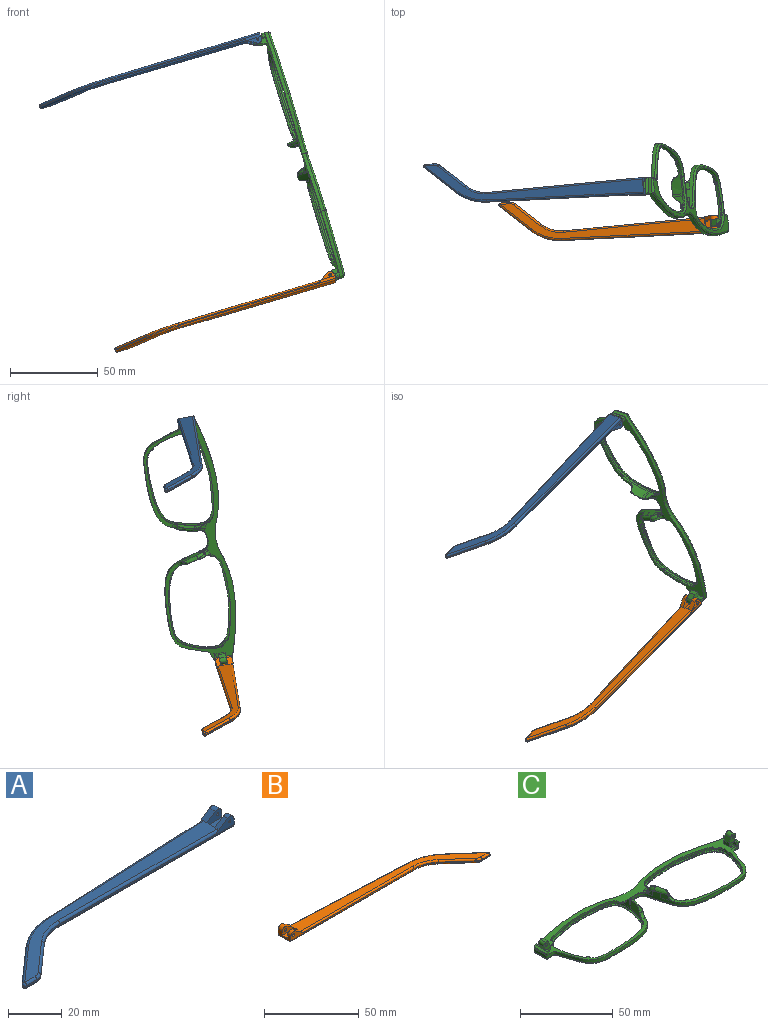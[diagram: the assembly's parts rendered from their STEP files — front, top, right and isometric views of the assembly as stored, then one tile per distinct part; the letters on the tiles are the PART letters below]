
ASSEMBLY  parts=3 mates=2
PART A: 43 faces, bbox 130.2x29.5x5.9 mm
  f0: plane 9.62x3.72mm, normal (1,0,0), area 24.7mm2, adj f1,f3,f4,f5,f10,f16,f18,f28
  f1: cylinder r=2.2mm len=3.45mm, axis (0,-1,0), area 11mm2, adj f0,f2,f4,f37
  f2: plane 6.01x3.91mm, normal (-0.55,0,0.84), area 12.7mm2, adj f1,f4,f9,f19,f37
  f3: plane 2.26x0.1mm, normal (0,0,1), area 0.1mm2, adj f0,f5,f18
  f4: plane 92.1x4.9mm, normal (0,-1,0), area 79.9mm2, adj f0,f1,f2,f14,f19,f36,f42
  f5: plane 93.42x4.13mm, normal (-0.04,1,0), area 64.8mm2, adj f0,f3,f11,f15,f17,f27,f28
  f6: plane 17.82x15.72mm, normal (-0.66,0.75,0), area 14.3mm2, adj f11,f12,f25,f30
  f7: plane 5.46x0.6mm, normal (0,-1,0), area 3.3mm2, adj f12,f13,f23,f32
  f8: plane 14.99x13.23mm, normal (0.66,-0.75,0), area 12mm2, adj f13,f14,f21,f34
  f9: plane 121.18x26.73mm, normal (0,0,1), area 627.7mm2, adj f2,f17,f19,f20,f21,f22,f23,f25
  f10: plane 129.1x27.08mm, normal (0,0,-1), area 686.5mm2, adj f0,f28,f29,f30,f32,f33,f34,f35
  f11: cylinder r=30mm len=18.52mm, axis (0,0,-1), area 12.2mm2, adj f5,f6,f26,f29
  f12: cylinder r=1mm len=1.75mm, axis (0,0,-1), area 1.5mm2, adj f6,f7,f24,f31
  f13: cylinder r=5mm len=3.31mm, axis (0,0,-1), area 2.2mm2, adj f7,f8,f22,f33
  f14: cylinder r=20mm len=13.23mm, axis (0,0,1), area 8.7mm2, adj f4,f8,f20,f35
  f15: plane 5.66x0.25mm, normal (0,0,-1), area 0.7mm2, adj f5,f17,f18
  f16: cylinder r=2.2mm len=3.45mm, axis (0,-1,0), area 14.8mm2, adj f0,f17,f18,f38
  f17: plane 6.01x3.91mm, normal (-0.55,0,0.84), area 16.9mm2, adj f5,f9,f15,f16,f18,f27,f38
  f18: plane 7.92x3.3mm, normal (0,1,0), area 15.9mm2, adj f0,f3,f15,f16,f17,f41
  f19: cylinder r=1mm len=84.18mm, axis (-1,0,0), area 131.4mm2, adj f2,f4,f9,f20
  f20: torus R=21mm, axis (0,0,1), area 23.1mm2, adj f9,f14,f19,f21
  f21: cylinder r=1mm len=15.65mm, axis (-0.75,-0.66,0), area 31.4mm2, adj f8,f9,f20,f22
  f22: torus R=4mm, axis (0,0,1), area 5.3mm2, adj f9,f13,f21,f23
  f23: cylinder r=1mm len=5.46mm, axis (-1,0,0), area 8.6mm2, adj f7,f9,f22,f24
  f24: sphere r=1mm, area 2.4mm2, adj f12,f23,f25
  f25: cylinder r=1mm len=18.48mm, axis (0.75,0.66,0), area 37.3mm2, adj f6,f9,f24,f26
  f26: torus R=29mm, axis (0,0,1), area 31.6mm2, adj f9,f11,f25,f27
  f27: cylinder r=1mm len=85.5mm, axis (1,0.04,0), area 133.5mm2, adj f5,f9,f17,f26
  f28: cylinder r=1mm len=93.46mm, axis (-1,-0.04,0), area 146.9mm2, adj f0,f5,f10,f29
  f29: torus R=29mm, axis (0,0,1), area 31.6mm2, adj f10,f11,f28,f30
  f30: cylinder r=1mm len=18.48mm, axis (-0.75,-0.66,0), area 37.3mm2, adj f6,f10,f29,f31
  f31: sphere r=1mm, area 2.4mm2, adj f12,f30,f32
  f32: cylinder r=1mm len=5.46mm, axis (1,0,0), area 8.6mm2, adj f7,f10,f31,f33
  f33: torus R=4mm, axis (0,0,1), area 5.3mm2, adj f10,f13,f32,f34
  f34: cylinder r=1mm len=15.65mm, axis (0.75,0.66,0), area 31.4mm2, adj f8,f10,f33,f35
  f35: torus R=21mm, axis (0,0,1), area 23.1mm2, adj f10,f14,f34,f36
  f36: cylinder r=1mm len=92.1mm, axis (1,0,0), area 144.7mm2, adj f0,f4,f10,f35
  f37: plane 7.92x4.7mm, normal (0,1,0), area 27mm2, adj f0,f1,f2,f39,f40,f42
  f38: plane 7.92x4.7mm, normal (0,-1,0), area 27mm2, adj f0,f16,f17,f39,f40,f41
  f39: plane 7.92x4.1mm, normal (0,0,1), area 32.5mm2, adj f0,f37,f38,f40
  f40: plane 4.1x1.4mm, normal (1,0,0), area 5.7mm2, adj f9,f37,f38,f39
  f41: cylinder r=0.5mm len=3.1mm, axis (0,-1,0), area 9.7mm2, adj f18,f38
  f42: cylinder r=0.5mm len=2.3mm, axis (0,-1,0), area 7.2mm2, adj f4,f37
PART B: 43 faces, bbox 130.2x29.5x5.9 mm
  f0: plane 9.62x3.72mm, normal (-1,0,0), area 24.7mm2, adj f1,f3,f4,f5,f10,f16,f18,f28
  f1: cylinder r=2.2mm len=3.45mm, axis (0,-1,0), area 11mm2, adj f0,f2,f4,f37
  f2: plane 6.01x3.91mm, normal (0.55,0,0.84), area 12.7mm2, adj f1,f4,f9,f19,f37
  f3: plane 2.26x0.1mm, normal (0,0,1), area 0.1mm2, adj f0,f5,f18
  f4: plane 92.1x4.9mm, normal (0,-1,0), area 78.2mm2, adj f0,f1,f2,f14,f19,f36,f42
  f5: plane 93.42x4.13mm, normal (0.04,1,0), area 64.8mm2, adj f0,f3,f11,f15,f17,f27,f28
  f6: plane 17.82x15.72mm, normal (0.66,0.75,0), area 14.3mm2, adj f11,f12,f25,f30
  f7: plane 5.46x0.6mm, normal (0,-1,0), area 3.3mm2, adj f12,f13,f23,f32
  f8: plane 14.99x13.23mm, normal (-0.66,-0.75,0), area 12mm2, adj f13,f14,f21,f34
  f9: plane 121.18x26.73mm, normal (0,0,1), area 627.7mm2, adj f2,f17,f19,f20,f21,f22,f23,f25
  f10: plane 129.1x27.08mm, normal (0,0,-1), area 686.5mm2, adj f0,f28,f29,f30,f32,f33,f34,f35
  f11: cylinder r=30mm len=18.52mm, axis (0,0,-1), area 12.2mm2, adj f5,f6,f26,f29
  f12: cylinder r=1mm len=1.75mm, axis (0,0,-1), area 1.5mm2, adj f6,f7,f24,f31
  f13: cylinder r=5mm len=3.31mm, axis (0,0,-1), area 2.2mm2, adj f7,f8,f22,f33
  f14: cylinder r=20mm len=13.23mm, axis (0,0,1), area 8.7mm2, adj f4,f8,f20,f35
  f15: plane 5.66x0.25mm, normal (0,0,-1), area 0.7mm2, adj f5,f17,f18
  f16: cylinder r=2.2mm len=3.45mm, axis (0,-1,0), area 14.8mm2, adj f0,f17,f18,f38
  f17: plane 6.01x3.91mm, normal (0.55,0,0.84), area 16.9mm2, adj f5,f9,f15,f16,f18,f27,f38
  f18: plane 7.92x3.3mm, normal (0,1,0), area 14.3mm2, adj f0,f3,f15,f16,f17,f41
  f19: cylinder r=1mm len=84.18mm, axis (1,0,0), area 131.4mm2, adj f2,f4,f9,f20
  f20: torus R=21mm, axis (0,0,1), area 23.1mm2, adj f9,f14,f19,f21
  f21: cylinder r=1mm len=15.65mm, axis (0.75,-0.66,0), area 31.4mm2, adj f8,f9,f20,f22
  f22: torus R=4mm, axis (0,0,1), area 5.3mm2, adj f9,f13,f21,f23
  f23: cylinder r=1mm len=5.46mm, axis (1,0,0), area 8.6mm2, adj f7,f9,f22,f24
  f24: sphere r=1mm, area 2.4mm2, adj f12,f23,f25
  f25: cylinder r=1mm len=18.48mm, axis (-0.75,0.66,0), area 37.3mm2, adj f6,f9,f24,f26
  f26: torus R=29mm, axis (0,0,1), area 31.6mm2, adj f9,f11,f25,f27
  f27: cylinder r=1mm len=85.5mm, axis (-1,0.04,0), area 133.5mm2, adj f5,f9,f17,f26
  f28: cylinder r=1mm len=93.46mm, axis (1,-0.04,0), area 146.9mm2, adj f0,f5,f10,f29
  f29: torus R=29mm, axis (0,0,1), area 31.6mm2, adj f10,f11,f28,f30
  f30: cylinder r=1mm len=18.48mm, axis (0.75,-0.66,0), area 37.3mm2, adj f6,f10,f29,f31
  f31: sphere r=1mm, area 2.4mm2, adj f12,f30,f32
  f32: cylinder r=1mm len=5.46mm, axis (-1,0,0), area 8.6mm2, adj f7,f10,f31,f33
  f33: torus R=4mm, axis (0,0,1), area 5.3mm2, adj f10,f13,f32,f34
  f34: cylinder r=1mm len=15.65mm, axis (-0.75,0.66,0), area 31.4mm2, adj f8,f10,f33,f35
  f35: torus R=21mm, axis (0,0,1), area 23.1mm2, adj f10,f14,f34,f36
  f36: cylinder r=1mm len=92.1mm, axis (-1,0,0), area 144.7mm2, adj f0,f4,f10,f35
  f37: plane 7.92x4.7mm, normal (0,1,0), area 25.4mm2, adj f0,f1,f2,f39,f40,f42
  f38: plane 7.92x4.7mm, normal (0,-1,0), area 25.4mm2, adj f0,f16,f17,f39,f40,f41
  f39: plane 7.92x4.1mm, normal (0,0,1), area 32.5mm2, adj f0,f37,f38,f40
  f40: plane 4.1x1.4mm, normal (-1,0,0), area 5.7mm2, adj f9,f37,f38,f39
  f41: cylinder r=0.88mm len=3.1mm, axis (0,-1,0), area 17mm2, adj f18,f38
  f42: cylinder r=0.88mm len=2.3mm, axis (0,-1,0), area 12.6mm2, adj f4,f37
PART C: 118 faces, bbox 148.1x40.9x17.9 mm
  f0: bspline ~1.82x1.22mm, area 0.7mm2, adj f2,f7,f37,f52
  f1: plane 147.69x40.46mm, normal (0,0,1), area 858.2mm2, adj f4,f5,f6,f7,f8,f12,f20,f23
  f2: bspline ~6.1x4.93mm, area 12.7mm2, adj f0,f7,f37,f41,f43,f52,f53
  f3: plane 4.46x1.45mm, normal (0,0,1), area 0.1mm2, adj f7,f38
  f4: plane 1.23x0.04mm, normal (0,0,1), area 0mm2, adj f1,f7,f22
  f5: plane 6.97x5.07mm, normal (0,1,0), area 22.7mm2, adj f1,f20,f21,f25,f27,f28,f30,f31
  f6: plane 3.2x2.36mm, normal (0,-1,0), area 5.7mm2, adj f1,f20,f26,f29
  f7: extruded ~73.26x39.84mm, area 292.7mm2, adj f0,f1,f2,f3,f4,f8,f13,f14
  f8: extruded ~35.39x5.69mm, area 72.2mm2, adj f1,f7,f18,f67
  f9: plane 144.78x37.85mm, normal (0,0,-1), area 582.4mm2, adj f13,f15,f17,f18,f19,f71,f73,f75
  f10: plane 56.06x35.45mm, normal (0,0,1), area 127mm2, adj f11,f19
  f11: extruded ~55.69x35.36mm, area 160.5mm2, adj f10,f12
  f12: extruded ~55.69x35.36mm, area 226.3mm2, adj f1,f11,f39,f40,f41,f42,f43,f44
  f13: bspline ~73.27x30.39mm, area 161.7mm2, adj f7,f9,f14,f71
  f14: bspline ~1x1mm, area 0.8mm2, adj f7,f13,f15
  f15: bspline ~8.99x1.23mm, area 12.6mm2, adj f7,f9,f14,f16
  f16: bspline ~1.04x1mm, area 0.7mm2, adj f7,f15,f17
  f17: bspline ~45.86x8.59mm, area 59.8mm2, adj f7,f9,f16,f18
  f18: bspline ~37.01x6.7mm, area 56.6mm2, adj f8,f9,f17,f76
  f19: bspline ~56.23x35.9mm, area 235.3mm2, adj f9,f10
  f20: plane 4x2.36mm, normal (-1,0,0), area 9.5mm2, adj f1,f5,f6,f21
  f21: plane 4x0.02mm, normal (0.34,0,0.94), area 0.1mm2, adj f5,f20,f28
  f22: plane 2.76x2.53mm, normal (0,-1,0), area 3.9mm2, adj f4,f26,f27,f35,f56
  f23: plane 7.67x1.6mm, normal (0.94,0,-0.34), area 13mm2, adj f1,f35,f36,f56
  f24: plane 2.1x1.69mm, normal (0,1,0), area 2.8mm2, adj f1,f25,f27,f36,f56
  f25: plane 3.3x2.1mm, normal (-1,0,0), area 6.9mm2, adj f1,f5,f24,f27
  f26: plane 2.35x2.1mm, normal (-1,0,0), area 4.9mm2, adj f1,f6,f22,f27,f29
  f27: plane 9.65x1.24mm, normal (0,0,1), area 8.2mm2, adj f5,f22,f24,f25,f26,f29,f30,f56
  f28: plane 4x3.31mm, normal (-0.94,0,0.34), area 14.1mm2, adj f5,f21,f29,f32
  f29: plane 5.77x5.06mm, normal (0,-1,0), area 17mm2, adj f6,f26,f27,f28,f30,f31,f32,f33
  f30: plane 4x2.21mm, normal (0.94,0,-0.34), area 9.4mm2, adj f5,f27,f29,f33
  f31: plane 4x0.01mm, normal (0.34,0,0.94), area 0mm2, adj f5,f29,f32,f33
  f32: cylinder r=1.98mm len=4mm, axis (0,1,0), area 12.4mm2, adj f5,f28,f29,f31
  f33: cylinder r=1.98mm len=4mm, axis (0,-1,0), area 12.4mm2, adj f5,f29,f30,f31
  f34: cylinder r=0.88mm len=4mm, axis (0,-1,0), area 22mm2, adj f5,f29
  f35: cone r=1mm half-angle=20deg, axis (0,0,1), area 2.3mm2, adj f1,f22,f23,f56
  f36: cylinder r=1mm len=2.28mm, axis (-0.34,0,-0.94), area 3mm2, adj f1,f23,f24,f56
  f37: extruded ~3.67x3.11mm, area 5.9mm2, adj f0,f2,f7,f59
  f38: extruded ~4.44x3.32mm, area 15.1mm2, adj f3,f7,f42,f43,f55
  f39: extruded ~4.98x1.37mm, area 6.6mm2, adj f12,f41
  f40: plane 3.63x0.97mm, normal (0,0,1), area 0.3mm2, adj f12,f41,f43
  f41: bspline ~15.5x15.35mm, area 6.4mm2, adj f2,f12,f39,f40,f54
  f42: bspline ~7.26x7.26mm, area 6.3mm2, adj f12,f38,f43,f55
  f43: bspline ~10.29x4.84mm, area 21.4mm2, adj f2,f7,f12,f38,f40,f42
  f44: plane 3.19x1.37mm, normal (0,0,-1), area 2.1mm2, adj f12,f45
  f45: cylinder r=2.28mm len=3.17mm, axis (0,0,1), area 2.1mm2, adj f1,f12,f44,f54
  f46: plane 3.14x2.79mm, normal (0,0,-1), area 3.9mm2, adj f12,f47
  f47: cylinder r=2.28mm len=3.13mm, axis (0,0,1), area 2.5mm2, adj f1,f12,f46
  f48: plane 1.79x1.31mm, normal (0,0,-1), area 0.9mm2, adj f12,f49
  f49: cylinder r=1.3mm len=1.78mm, axis (0,0,1), area 1.3mm2, adj f1,f12,f48
  f50: plane 1.95x1.68mm, normal (0,0,-1), area 1.5mm2, adj f12,f51
  f51: cylinder r=1.3mm len=1.93mm, axis (0,0,1), area 1.5mm2, adj f1,f12,f50
  f52: bspline ~2.66x2.04mm, area 1.9mm2, adj f0,f2,f7,f53,f58
  f53: bspline ~3.55x3.47mm, area 3.7mm2, adj f1,f2,f52,f54,f58
  f54: bspline ~6.16x4.45mm, area 7.9mm2, adj f1,f12,f41,f45,f53
  f55: bspline ~3.7x3.66mm, area 7.8mm2, adj f1,f7,f12,f38,f42
  f56: plane 9.71x1.44mm, normal (0.34,0,0.94), area 13.9mm2, adj f22,f23,f24,f27,f35,f36
  f57: bspline ~6.38x2.14mm, area 2.6mm2, adj f1,f7,f58,f115
  f58: bspline ~2.1x1.46mm, area 0.6mm2, adj f7,f52,f53,f57
  f59: bspline ~5.24x1.75mm, area 0mm2, adj f7,f37
  f60: bspline ~2.19x1.4mm, area 0.7mm2, adj f61,f66,f95,f110
  f61: bspline ~6.1x4.93mm, area 12.6mm2, adj f60,f66,f95,f99,f101,f110,f111
  f62: plane 4.46x1.45mm, normal (0,0,1), area 0.1mm2, adj f66,f96
  f63: plane 1.23x0.04mm, normal (0,0,1), area 0mm2, adj f1,f66,f80
  f64: plane 6.97x5.07mm, normal (0,1,0), area 22.7mm2, adj f1,f78,f79,f83,f85,f86,f88,f89
  f65: plane 3.2x2.36mm, normal (0,-1,0), area 5.7mm2, adj f1,f78,f84,f87
  f66: extruded ~73.26x39.84mm, area 292.7mm2, adj f1,f7,f60,f61,f62,f63,f67,f71
  f67: extruded ~35.39x5.69mm, area 72.2mm2, adj f1,f8,f66,f76
  f68: plane 56.06x35.45mm, normal (0,0,1), area 127mm2, adj f69,f77
  f69: extruded ~55.69x35.36mm, area 160.5mm2, adj f68,f70
  f70: extruded ~55.69x35.36mm, area 226.4mm2, adj f1,f69,f97,f98,f99,f100,f101,f102
  f71: bspline ~73.83x30.39mm, area 161.7mm2, adj f9,f13,f66,f72
  f72: bspline ~1x1mm, area 0.8mm2, adj f66,f71,f73
  f73: bspline ~8.99x1.23mm, area 12.6mm2, adj f9,f66,f72,f74
  f74: bspline ~1.04x1mm, area 0.8mm2, adj f66,f73,f75
  f75: bspline ~45.86x8.59mm, area 59.8mm2, adj f9,f66,f74,f76
  f76: bspline ~37.01x6.7mm, area 56.6mm2, adj f9,f18,f67,f75
  f77: bspline ~56.22x35.9mm, area 235.3mm2, adj f9,f68
  f78: plane 4x2.36mm, normal (1,0,0), area 9.5mm2, adj f1,f64,f65,f79
  f79: plane 4x0.02mm, normal (-0.34,0,0.94), area 0.1mm2, adj f64,f78,f86
  f80: plane 2.76x2.53mm, normal (0,-1,0), area 3.9mm2, adj f63,f84,f85,f93,f114
  f81: plane 7.67x1.6mm, normal (-0.94,0,-0.34), area 13mm2, adj f1,f93,f94,f114
  f82: plane 2.1x1.69mm, normal (0,1,0), area 2.8mm2, adj f1,f83,f85,f94,f114
  f83: plane 3.3x2.1mm, normal (1,0,0), area 6.9mm2, adj f1,f64,f82,f85
  f84: plane 2.35x2.1mm, normal (1,0,0), area 4.9mm2, adj f1,f65,f80,f85,f87
  f85: plane 9.65x1.24mm, normal (0,0,1), area 8.2mm2, adj f64,f80,f82,f83,f84,f87,f88,f114
  f86: plane 4x3.31mm, normal (0.94,0,0.34), area 14.1mm2, adj f64,f79,f87,f90
  f87: plane 5.77x5.06mm, normal (0,-1,0), area 17mm2, adj f65,f84,f85,f86,f88,f89,f90,f91
  f88: plane 4x2.21mm, normal (-0.94,0,-0.34), area 9.4mm2, adj f64,f85,f87,f91
  f89: plane 4x0.01mm, normal (-0.34,0,0.94), area 0mm2, adj f64,f87,f90,f91
  f90: cylinder r=1.98mm len=4mm, axis (0,1,0), area 12.4mm2, adj f64,f86,f87,f89
  f91: cylinder r=1.98mm len=4mm, axis (0,-1,0), area 12.4mm2, adj f64,f87,f88,f89
  f92: cylinder r=0.88mm len=4mm, axis (0,-1,0), area 22mm2, adj f64,f87
  f93: cone r=1mm half-angle=20deg, axis (0,0,1), area 2.3mm2, adj f1,f80,f81,f114
  f94: cylinder r=1mm len=2.28mm, axis (0.34,0,-0.94), area 3mm2, adj f1,f81,f82,f114
  f95: extruded ~3.67x3.11mm, area 5.9mm2, adj f60,f61,f66,f117
  f96: extruded ~4.44x3.32mm, area 15.1mm2, adj f62,f66,f100,f101,f113
  f97: extruded ~4.98x1.36mm, area 6.6mm2, adj f70,f99
  f98: plane 3.63x0.97mm, normal (0,0,1), area 0.3mm2, adj f70,f99,f101
  f99: bspline ~15.5x15.35mm, area 6.4mm2, adj f61,f70,f97,f98,f112
  f100: bspline ~7.26x7.26mm, area 6.2mm2, adj f70,f96,f101,f113
  f101: bspline ~10.29x4.84mm, area 21.5mm2, adj f61,f66,f70,f96,f98,f100
  f102: plane 3.19x1.37mm, normal (0,0,-1), area 2.1mm2, adj f70,f103
  f103: cylinder r=2.28mm len=3.17mm, axis (0,0,1), area 2.1mm2, adj f1,f70,f102,f112
  f104: plane 3.14x2.79mm, normal (0,0,-1), area 3.9mm2, adj f70,f105
  f105: cylinder r=2.28mm len=3.13mm, axis (0,0,1), area 2.5mm2, adj f1,f70,f104
  f106: plane 1.79x1.31mm, normal (0,0,-1), area 0.9mm2, adj f70,f107
  f107: cylinder r=1.3mm len=1.78mm, axis (0,0,1), area 1.3mm2, adj f1,f70,f106
  f108: plane 1.95x1.68mm, normal (0,0,-1), area 1.5mm2, adj f70,f109
  f109: cylinder r=1.3mm len=1.93mm, axis (0,0,1), area 1.5mm2, adj f1,f70,f108
  f110: bspline ~2.65x2.03mm, area 1.9mm2, adj f60,f61,f66,f111,f116
  f111: bspline ~3.55x3.47mm, area 3.7mm2, adj f1,f61,f110,f112,f116
  f112: bspline ~5.94x4.42mm, area 7.9mm2, adj f1,f70,f99,f103,f111
  f113: bspline ~3.7x3.66mm, area 7.8mm2, adj f1,f66,f70,f96,f100
  f114: plane 9.71x1.44mm, normal (-0.34,0,0.94), area 13.9mm2, adj f80,f81,f82,f85,f93,f94
  f115: bspline ~6.38x2.14mm, area 2.6mm2, adj f1,f57,f66,f116
  f116: bspline ~2.1x1.46mm, area 0.6mm2, adj f66,f110,f111,f115
  f117: bspline ~5.24x1.75mm, area 0mm2, adj f66,f95
PLACE A rot(axis=(0.99,0.03,0.15),170.8deg) t=(-72.91,149.83,447.51)mm
PLACE B rot(axis=(0.15,-0.08,-0.99),176deg) t=(88.94,139.09,341.04)mm
PLACE C rot(axis=(0.8,-0.03,-0.6),170.7deg) t=(12.8,140.36,396.4)mm
MATE revolute A.f1 <-> C.f90  axis (-0.04,0.98,-0.17) through (-14.47,146.41,462.2)mm
MATE revolute B.f41 <-> C.f33  axis (-0.04,0.98,-0.17) through (27.06,125.44,327.94)mm
